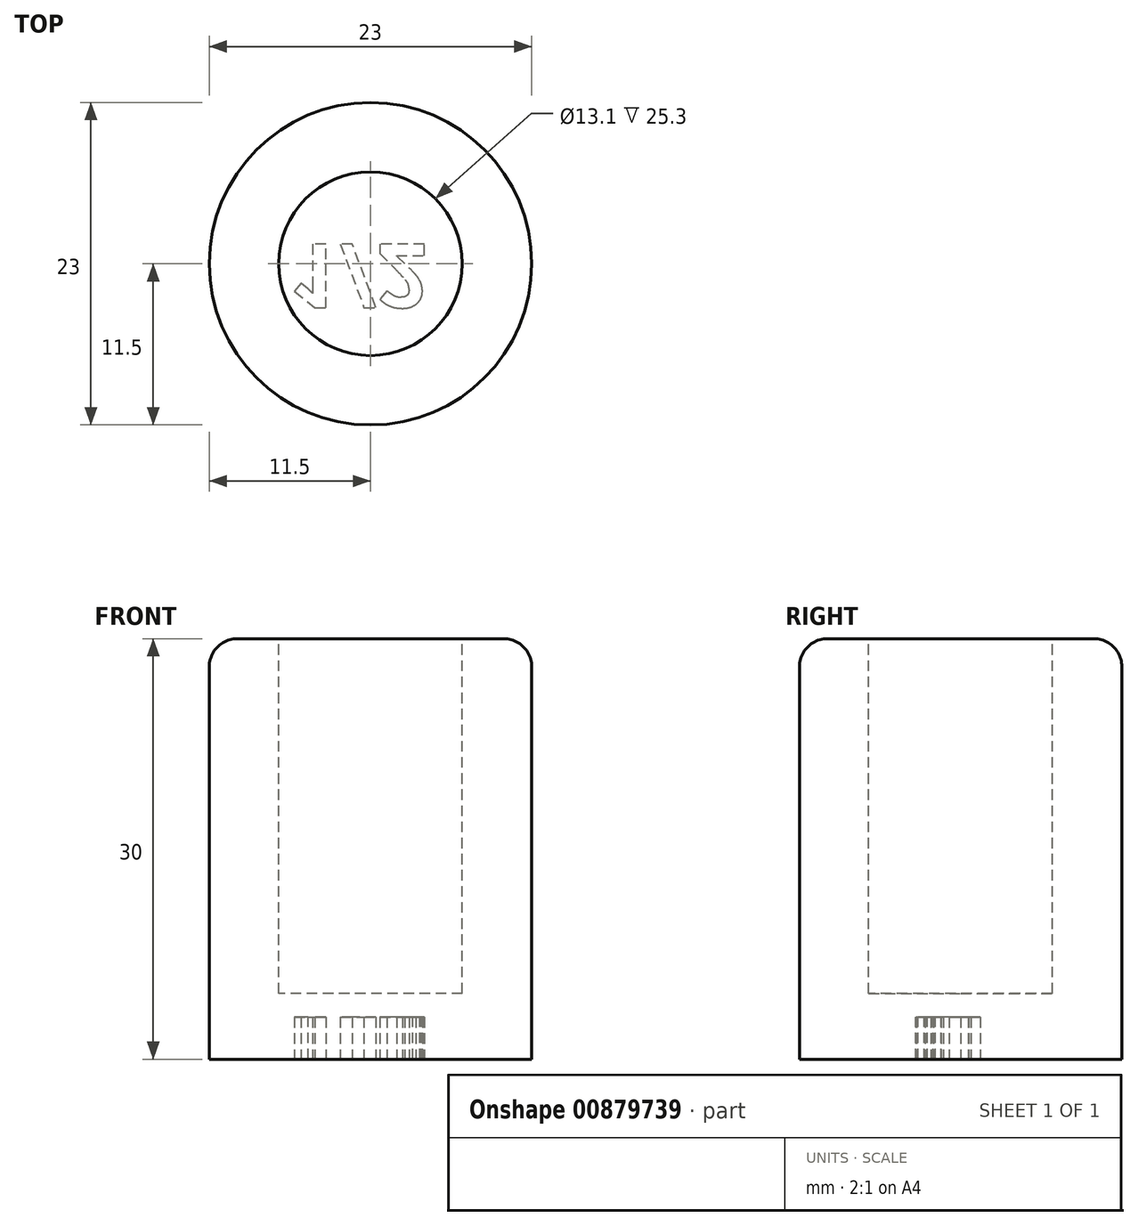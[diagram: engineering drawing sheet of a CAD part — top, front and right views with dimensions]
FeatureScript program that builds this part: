
annotation { "Feature Type Name" : "Feature", "Feature Type Description" : "" }
export const myFeature = defineFeature(function(context is Context, id is Id, definition is map)
    precondition{}
    {
        {
            var Q0;
            Q0=qCreatedBy(makeId("Top.planeOp"),FACE);
            var sketch = newSketch(context, id + "F0", { "sketchPlane" : qUnion([Q0])});
            skCircle(sketch, "E0", {"center": v(0, 0) * mm, "radius": 11.5 * mm});
            skSolve(sketch);
        }
        {
            var Q0;
            Q0=makeQuery(id+"F0.imprint","IMPRINT",FACE,{"disambiguationData":[TD([[makeQuery(id+"F0.imprint","IMPRINT",EDGE,{"derivedFrom":sQuery(id+"F0.wireOp",EDGE,"E0")}),1.0]])]});
            extrude(context, id + "F1", {"entities" : qUnion([Q0]), "depth" : 30 * mm, "offsetDistance" : 25 * mm});
        }
        {
            var Q0;
            Q0=makeQuery(id+"F1.opExtrude","CAP_FACE",FACE,{"disambiguationData":[OSD([sQuery(id+"F0.wireOp",EDGE,"E0")])],"isStart":false});
            cPlane(context, id + "F2", {"entities" : qUnion([Q0]), "cplaneType" : CPlaneType.OFFSET, "offset" : 0 * mm, "width" : 150 * mm, "height" : 150 * mm});
        }
        {
            var Q0;
            Q0=qCreatedBy(id+"F2.planeOp",FACE);
            var sketch = newSketch(context, id + "F3", { "sketchPlane" : qUnion([Q0])});
            skCircle(sketch, "E1", {"center": v(0, 0) * mm, "radius": 6.55 * mm});
            skSolve(sketch);
        }
        {
            var Q0;
            Q0=qSketchRegion(id+"F3",true);
            extrude(context, id + "F4", {"entities" : qUnion([Q0]), "operationType" : NewBodyOperationType.REMOVE, "oppositeDirection" : true, "depth" : 25.3 * mm, "offsetDistance" : 25 * mm});
        }
        {
            var Q0;
            Q0=makeQuery(id+"F1.opExtrude","CAP_FACE",FACE,{"disambiguationData":[OSD([sQuery(id+"F0.wireOp",EDGE,"E0")])],"isStart":true});
            cPlane(context, id + "F5", {"entities" : qUnion([Q0]), "cplaneType" : CPlaneType.OFFSET, "offset" : 0 * mm, "width" : 150 * mm, "height" : 150 * mm});
        }
        {
            var Q0;
            Q0=qCreatedBy(id+"F5.planeOp",FACE);
            var sketch = newSketch(context, id + "F6", { "sketchPlane" : qUnion([Q0])});
            skLineSegment(sketch, "E2", {"start": v(7.64, 3.16) * mm, "end": v(-6.76, 3.16) * mm, "construction": true});
            skText(sketch, "E3", { "text": "1/2", "fontName": "OpenSans-Bold.ttf"});
            const initialGuessF6  = {"E3": [-0.0058, -0.00139, 1, 0, 0.00455]};
            skSetInitialGuess(sketch, initialGuessF6);
            skSolve(sketch);
        }
        {
            var Q0;
            Q0=qSketchRegion(id+"F6",true);
            extrude(context, id + "F7", {"entities" : qUnion([Q0]), "operationType" : NewBodyOperationType.REMOVE, "oppositeDirection" : true, "depth" : 3 * mm, "offsetDistance" : 25 * mm});
        }
        {
            var Q0;
            Q0=makeQuery(id+"F1.opExtrude","CAP_EDGE",EDGE,{"disambiguationData":[OSD([sQuery(id+"F0.wireOp",EDGE,"E0")])],"isStart":false});
            fillet(context, id + "F8", {"entities" : qUnion([Q0]), "radius" : 2 * mm, "tangentPropagation" : true, "allowEdgeOverflow" : false});
        }
    });
